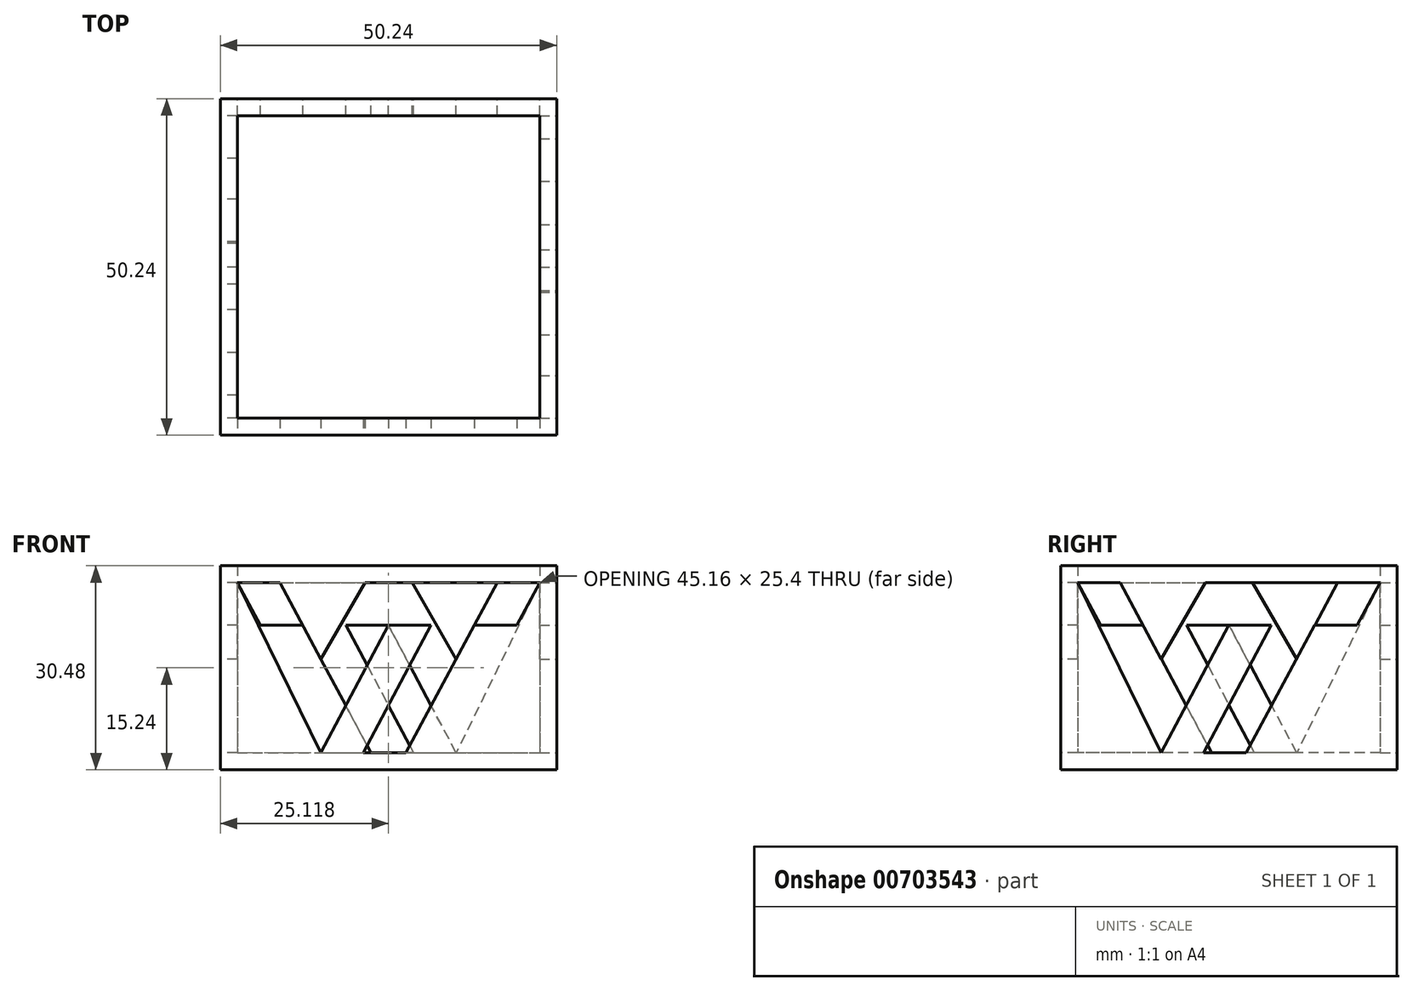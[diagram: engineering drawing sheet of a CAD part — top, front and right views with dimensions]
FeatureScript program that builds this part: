
annotation { "Feature Type Name" : "Feature", "Feature Type Description" : "" }
export const myFeature = defineFeature(function(context is Context, id is Id, definition is map)
    precondition{}
    {
        {
            var Q0;
            Q0=qCreatedBy(makeId("Front.planeOp"),FACE);
            var sketch = newSketch(context, id + "F0", { "sketchPlane" : qUnion([Q0])});
            skLineSegment(sketch, "E0", {"start": v(-15.3, 25.4) * mm, "end": v(-2.83, 0) * mm});
            skLineSegment(sketch, "E1", {"start": v(-2.83, 0) * mm, "end": v(7.28, 19.05) * mm});
            skLineSegment(sketch, "E2", {"start": v(7.28, 19.05) * mm, "end": v(13.63, 19.05) * mm});
            skLineSegment(sketch, "E3", {"start": v(13.63, 19.05) * mm, "end": v(3.52, 0) * mm});
            skLineSegment(sketch, "E4", {"start": v(3.52, 0) * mm, "end": v(9.87, 0) * mm});
            skLineSegment(sketch, "E5", {"start": v(9.87, 0) * mm, "end": v(20.09, 19.05) * mm});
            skLineSegment(sketch, "E6", {"start": v(20.09, 19.05) * mm, "end": v(26.44, 19.05) * mm});
            skLineSegment(sketch, "E7", {"start": v(26.44, 19.05) * mm, "end": v(29.87, 25.4) * mm});
            skLineSegment(sketch, "E8", {"start": v(29.87, 25.4) * mm, "end": v(3.76, 25.4) * mm});
            skLineSegment(sketch, "E9", {"start": v(3.76, 25.4) * mm, "end": v(-2.83, 13.97) * mm});
            skLineSegment(sketch, "E10", {"start": v(-2.83, 13.97) * mm, "end": v(-8.94, 25.4) * mm});
            skLineSegment(sketch, "E11", {"start": v(-8.94, 25.4) * mm, "end": v(-15.3, 25.4) * mm});
            skSolve(sketch);
        }
        {
            var Q0;
            Q0=qCreatedBy(makeId("Front.planeOp"),FACE);
            var sketch = newSketch(context, id + "F1", { "sketchPlane" : qUnion([Q0])});
            skLineSegment(sketch, "E12.bottom", {"start": v(-17.83, 27.94) * mm, "end": v(32.4, 27.94) * mm});
            skLineSegment(sketch, "E12.top", {"start": v(-17.83, -2.54) * mm, "end": v(32.4, -2.54) * mm});
            skLineSegment(sketch, "E12.left", {"start": v(-17.83, 27.94) * mm, "end": v(-17.83, -2.54) * mm});
            skLineSegment(sketch, "E12.right", {"start": v(32.4, 27.94) * mm, "end": v(32.4, -2.54) * mm});
            skSolve(sketch);
        }
        {
            var Q0;
            Q0=makeQuery(id+"F1.imprint","IMPRINT",FACE,{"disambiguationData":[TD([[makeQuery(id+"F1.imprint","IMPRINT",EDGE,{"derivedFrom":sQuery(id+"F1.wireOp",EDGE,"E12.bottom")}),-1.0]])]});
            extrude(context, id + "F2", {"entities" : qUnion([Q0]), "oppositeDirection" : true, "depth" : 50.24 * mm, "offsetDistance" : 25.4 * mm});
        }
        {
            var Q0;
            Q0=makeQuery(id+"F2.opExtrude","SWEPT_FACE",FACE,{"disambiguationData":[OSD([sQuery(id+"F1.wireOp",EDGE,"E12.right")])]});
            var sketch = newSketch(context, id + "F3", { "sketchPlane" : qUnion([Q0])});
            skLineSegment(sketch, "E13", {"start": v(2.54, 25.4) * mm, "end": v(15, 0) * mm});
            skLineSegment(sketch, "E14", {"start": v(15, 0) * mm, "end": v(25.11, 19.05) * mm});
            skLineSegment(sketch, "E15", {"start": v(25.11, 19.05) * mm, "end": v(31.46, 19.05) * mm});
            skLineSegment(sketch, "E16", {"start": v(31.46, 19.05) * mm, "end": v(21.35, 0) * mm});
            skLineSegment(sketch, "E17", {"start": v(21.35, 0) * mm, "end": v(27.7, 0) * mm});
            skLineSegment(sketch, "E18", {"start": v(27.7, 0) * mm, "end": v(37.92, 19.05) * mm});
            skLineSegment(sketch, "E19", {"start": v(37.92, 19.05) * mm, "end": v(44.27, 19.05) * mm});
            skLineSegment(sketch, "E20", {"start": v(44.27, 19.05) * mm, "end": v(47.7, 25.4) * mm});
            skLineSegment(sketch, "E21", {"start": v(47.7, 25.4) * mm, "end": v(21.6, 25.4) * mm});
            skLineSegment(sketch, "E22", {"start": v(21.6, 25.4) * mm, "end": v(15, 13.97) * mm});
            skLineSegment(sketch, "E23", {"start": v(15, 13.97) * mm, "end": v(8.9, 25.4) * mm});
            skLineSegment(sketch, "E24", {"start": v(8.9, 25.4) * mm, "end": v(2.54, 25.4) * mm});
            skSolve(sketch);
        }
        {
            var Q0;
            Q0=makeQuery(id+"F2.opExtrude","SWEPT_FACE",FACE,{"disambiguationData":[OSD([sQuery(id+"F1.wireOp",EDGE,"E12.bottom")])]});
            var Q1;
            Q1=makeQuery(id+"F2.opExtrude","SWEPT_BODY",BODY,{"disambiguationData":[OSD([sQuery(id+"F1.wireOp",EDGE,"E12.bottom"),sQuery(id+"F1.wireOp",EDGE,"E12.top"),sQuery(id+"F1.wireOp",EDGE,"E12.left"),sQuery(id+"F1.wireOp",EDGE,"E12.right")])]});
            shell(context, id + "F4", {"entities" : qUnion([Q0]), "parts" : qUnion([Q1]), "thickness" : 2.54 * mm});
        }
        {
            var Q0;
            Q0=makeQuery(id+"F2.opExtrude","CAP_FACE",FACE,{"disambiguationData":[OSD([sQuery(id+"F1.wireOp",EDGE,"E12.bottom"),sQuery(id+"F1.wireOp",EDGE,"E12.top"),sQuery(id+"F1.wireOp",EDGE,"E12.left"),sQuery(id+"F1.wireOp",EDGE,"E12.right")])],"isStart":false});
            var sketch = newSketch(context, id + "F5", { "sketchPlane" : qUnion([Q0])});
            skLineSegment(sketch, "E25", {"start": v(-29.87, 25.4) * mm, "end": v(-17.4, 0) * mm});
            skLineSegment(sketch, "E26", {"start": v(-17.4, 0) * mm, "end": v(-7.3, 19.05) * mm});
            skLineSegment(sketch, "E27", {"start": v(-7.3, 19.05) * mm, "end": v(-0.94, 19.05) * mm});
            skLineSegment(sketch, "E28", {"start": v(-0.94, 19.05) * mm, "end": v(-11.06, 0) * mm});
            skLineSegment(sketch, "E29", {"start": v(-11.06, 0) * mm, "end": v(-4.7, 0) * mm});
            skLineSegment(sketch, "E30", {"start": v(-4.7, 0) * mm, "end": v(5.51, 19.05) * mm});
            skLineSegment(sketch, "E31", {"start": v(5.51, 19.05) * mm, "end": v(11.86, 19.05) * mm});
            skLineSegment(sketch, "E32", {"start": v(11.86, 19.05) * mm, "end": v(15.3, 25.4) * mm});
            skLineSegment(sketch, "E33", {"start": v(15.3, 25.4) * mm, "end": v(-10.82, 25.4) * mm});
            skLineSegment(sketch, "E34", {"start": v(-10.82, 25.4) * mm, "end": v(-17.4, 13.97) * mm});
            skLineSegment(sketch, "E35", {"start": v(-17.4, 13.97) * mm, "end": v(-23.52, 25.4) * mm});
            skLineSegment(sketch, "E36", {"start": v(-23.52, 25.4) * mm, "end": v(-29.87, 25.4) * mm});
            skSolve(sketch);
        }
        {
            var Q0;
            Q0=makeQuery(id+"F2.opExtrude","SWEPT_FACE",FACE,{"disambiguationData":[OSD([sQuery(id+"F1.wireOp",EDGE,"E12.left")])]});
            var sketch = newSketch(context, id + "F6", { "sketchPlane" : qUnion([Q0])});
            skLineSegment(sketch, "E37", {"start": v(-47.7, 25.4) * mm, "end": v(-35.24, 0) * mm});
            skLineSegment(sketch, "E38", {"start": v(-35.24, 0) * mm, "end": v(-25.13, 19.05) * mm});
            skLineSegment(sketch, "E39", {"start": v(-25.13, 19.05) * mm, "end": v(-18.78, 19.05) * mm});
            skLineSegment(sketch, "E40", {"start": v(-18.78, 19.05) * mm, "end": v(-28.89, 0) * mm});
            skLineSegment(sketch, "E41", {"start": v(-28.89, 0) * mm, "end": v(-22.54, 0) * mm});
            skLineSegment(sketch, "E42", {"start": v(-22.54, 0) * mm, "end": v(-12.32, 19.05) * mm});
            skLineSegment(sketch, "E43", {"start": v(-12.32, 19.05) * mm, "end": v(-5.97, 19.05) * mm});
            skLineSegment(sketch, "E44", {"start": v(-5.97, 19.05) * mm, "end": v(-2.54, 25.4) * mm});
            skLineSegment(sketch, "E45", {"start": v(-2.54, 25.4) * mm, "end": v(-28.65, 25.4) * mm});
            skLineSegment(sketch, "E46", {"start": v(-28.65, 25.4) * mm, "end": v(-35.24, 13.97) * mm});
            skLineSegment(sketch, "E47", {"start": v(-35.24, 13.97) * mm, "end": v(-41.35, 25.4) * mm});
            skLineSegment(sketch, "E48", {"start": v(-41.35, 25.4) * mm, "end": v(-47.7, 25.4) * mm});
            skSolve(sketch);
        }
        {
            var Q0;
            Q0 = qSketchRegion(id + "F0", true);
            extrude(context, id + "F7", {"entities" : qUnion([Q0]), "operationType" : NewBodyOperationType.REMOVE, "oppositeDirection" : true, "depth" : 2.54 * mm, "offsetDistance" : 25.4 * mm});
        }
        {
            var Q0;
            Q0=makeQuery(id+"F6.imprint","IMPRINT",FACE,{"disambiguationData":[TD([[makeQuery(id+"F6.imprint","IMPRINT",EDGE,{"derivedFrom":sQuery(id+"F6.wireOp",EDGE,"E37")}),1.0]])]});
            extrude(context, id + "F8", {"entities" : qUnion([Q0]), "operationType" : NewBodyOperationType.REMOVE, "oppositeDirection" : true, "depth" : 2.54 * mm, "offsetDistance" : 25.4 * mm});
        }
        {
            var Q0;
            Q0=makeQuery(id+"F5.imprint","IMPRINT",FACE,{"disambiguationData":[TD([[makeQuery(id+"F5.imprint","IMPRINT",EDGE,{"derivedFrom":sQuery(id+"F5.wireOp",EDGE,"E25")}),1.0]])]});
            extrude(context, id + "F9", {"entities" : qUnion([Q0]), "operationType" : NewBodyOperationType.REMOVE, "oppositeDirection" : true, "depth" : 2.54 * mm, "offsetDistance" : 25.4 * mm});
        }
        {
            var Q0;
            Q0=makeQuery(id+"F3.imprint","IMPRINT",FACE,{"disambiguationData":[TD([[makeQuery(id+"F3.imprint","IMPRINT",EDGE,{"derivedFrom":sQuery(id+"F3.wireOp",EDGE,"E13")}),1.0]])]});
            extrude(context, id + "F10", {"entities" : qUnion([Q0]), "operationType" : NewBodyOperationType.REMOVE, "oppositeDirection" : true, "depth" : 2.54 * mm, "offsetDistance" : 25.4 * mm});
        }
    });
